# Revit family: КБ РАШВОРК  арт.347.rfa
name_source: partatom
category: Арматура трубопроводов
units: mm (PartAtom-declared; Revit-internal decimal feet)

## family parameters
Всегда вертикально = Нет
На основе рабочей плоскости = Нет
Общий = Нет
При загрузке вырезать с полостями = Да
Размер круглого соединителя = Использовать диаметр
Тип детали = Нормальный

## types (10) — shared parameters
ADSK_Единица измерения = шт
ADSK_Завод-изготовитель = ООО "ТД "РАШВОРК"
URL = https://rwru.ru
Изготовитель = ООО "ТД "РАШВОРК"
Корпус = чугун GJL-250 (GG25)
Маховик = Нейлон
УГОЛ = 90.00°
zero-valued in all types: Отметка по умолчанию

## per-type parameters (varying)
| type | ADSK_Код изделия | ADSK_Масса | D1 | H1 | H2 | H3 | H4 | HHH | L | LH1 | LH2 | LH3 | LH4 | LLL | Lнакл | R | W | b | d | f | Соединитель | Уго_длинна | Управление |
| Клапан балансировочный РАШВОРК 347-040-16, DN040, PN16, корпус - чугун GJS-400-15 (GGG40), клапан - нерж. сталь CF8, уплотнение - EPDM, Ф/Ф | 347-040-16 | 10.5 | 70 мм | 30 мм | 24 мм | 32 мм | 44 мм | 216 мм | 230 мм | 39 мм | 63 мм | 44 мм | 57 мм | 25 мм | 85 мм | 84 мм | 150 мм | 18 мм | 50 мм | 3 мм | 40 мм | 230 мм | Маховик : Ручка 1 |
| Клапан балансировочный РАШВОРК 347-300-16, DN300, PN16, корпус - чугун GJS-400-15 (GGG40), клапан - нерж. сталь CF8, уплотнение - EPDM, Ф/Ф | 347-300-16 | 200 | 370 мм | 94 мм | 47 мм | 119 мм | 170 мм | 216 мм | 850 мм | 160 мм | 203 мм | 164 мм | 210 мм | 38 мм | 285 мм | 370 мм | 460 мм | 25 мм | 300 мм | 4 мм | 300 мм | 850 мм | Маховик : Ручка 2 |
| Клапан балансировочный РАШВОРК 347-050-16, DN050, PN16, корпус - чугун GJS-400-15 (GGG40), клапан - нерж. сталь CF8, уплотнение - EPDM, Ф/Ф | 347-050-16 | 10.5 | 70 мм | 30 мм | 24 мм | 32 мм | 44 мм | 216 мм | 230 мм | 39 мм | 63 мм | 44 мм | 57 мм | 25 мм | 85 мм | 99 мм | 150 мм | 15 мм | 50 мм | 3 мм | 50 мм | 230 мм | Маховик : Ручка 1 |
| Клапан балансировочный РАШВОРК 347-065-16, DN065, PN16, корпус - чугун GJS-400-15 (GGG40), клапан - нерж. сталь CF8, уплотнение - EPDM, Ф/Ф | 347-065-16 | 15 | 102 мм | 35 мм | 21 мм | 30 мм | 60 мм | 216 мм | 290 мм | 39 мм | 65 мм | 47 мм | 68 мм | 25 мм | 95 мм | 120 мм | 185 мм | 19 мм | 65 мм | 3 мм | 65 мм | 290 мм | Маховик : Ручка 1 |
| Клапан балансировочный РАШВОРК 347-080-16, DN080, PN16, корпус - чугун GJS-400-15 (GGG40), клапан - нерж. сталь CF8, уплотнение - EPDM, Ф/Ф | 347-080-16 | 19.5 | 132 мм | 35 мм | 25 мм | 32 мм | 65 мм | 216 мм | 310 мм | 50 мм | 72 мм | 60 мм | 70 мм | 38 мм | 105 мм | 132 мм | 200 мм | 19 мм | 80 мм | 3 мм | 80 мм | 310 мм | Маховик : Ручка 1 |
| Клапан балансировочный РАШВОРК 347-100-16, DN100, PN16, корпус - чугун GJS-400-15 (GGG40), клапан - нерж. сталь CF8, уплотнение - EPDM, Ф/Ф | 347-100-16 | 28 | 148 мм | 44 мм | 28 мм | 50 мм | 70 мм | 100 мм | 350 мм | 60 мм | 90 мм | 70 мм | 85 мм | 350 мм | 108 мм | 156 мм | 220 мм | 19 мм | 100 мм | 3 мм | 100 мм | 350 мм | Маховик : Ручка 1 |
| Клапан балансировочный РАШВОРК 347-125-16, DN125, PN16, корпус - чугун GJS-400-15 (GGG40), клапан - нерж. сталь CF8, уплотнение - EPDM, Ф/Ф | 347-125-16 | 37.5 | 170 мм | 43 мм | 35 мм | 50 мм | 82 мм | 216 мм | 400 мм | 75 мм | 100 мм | 81 мм | 100 мм | 38 мм | 125 мм | 184 мм | 250 мм | 19 мм | 125 мм | 3 мм | 125 мм | 400 мм | Маховик : Ручка 1 |
| Клапан балансировочный РАШВОРК 347-150-16, DN150, PN16, корпус - чугун GJS-400-15 (GGG40), клапан - нерж. сталь CF8, уплотнение - EPDM, Ф/Ф | 347-150-16 | 52.5 | 176 мм | 47 мм | 34 мм | 75 мм | 81 мм | 216 мм | 480 мм | 86 мм | 120 мм | 95 мм | 119 мм | 38 мм | 150 мм | 211 мм | 285 мм | 19 мм | 150 мм | 3 мм | 150 мм | 480 мм | Маховик : Ручка 1 |
| Клапан балансировочный РАШВОРК 347-200-16, DN200, PN16, корпус - чугун GJS-400-15 (GGG40), клапан - нерж. сталь CF8, уплотнение - EPDM, Ф/Ф | 347-200-16 | 99 | 254 мм | 84 мм | 40 мм | 83 мм | 135 мм | 216 мм | 600 мм | 112 мм | 155 мм | 125 мм | 147 мм | 38 мм | 186 мм | 266 мм | 340 мм | 20 мм | 200 мм | 3 мм | 200 мм | 600 мм | Маховик : Ручка 2 |
| Клапан балансировочный РАШВОРК 347-250-16, DN250, PN16, корпус - чугун GJS-400-15 (GGG40), клапан - нерж. сталь CF8, уплотнение - EPDM, Ф/Ф | 347-250-16 | 146 | 310 мм | 84 мм | 50 мм | 105 мм | 150 мм | 216 мм | 730 мм | 150 мм | 183 мм | 153 мм | 183 мм | 38 мм | 245 мм | 319 мм | 405 мм | 22 мм | 250 мм | 3 мм | 250 мм | 730 мм | Маховик : Ручка 2 |

note: column(s) folded — value = type name in every type: ADSK_Наименование
